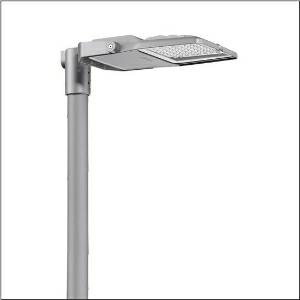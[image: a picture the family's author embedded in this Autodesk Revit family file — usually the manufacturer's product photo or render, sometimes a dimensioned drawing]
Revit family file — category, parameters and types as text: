
# Revit family: floodlight_fl_21_mini___pl33t_5xa7771d4f3a_f110
name_source: partatom
category: Lighting Fixtures
units: mm (PartAtom-declared; Revit-internal decimal feet)

## family parameters
Cut with Voids When Loaded = No
Host = Face
Light Source = No
Part Type = Normal
Room Calculation Point = No
Round Connector Dimension = Use Diameter
Shared = No

## types (1)
- --- (1 x LED, 18390 lm, 143 W, 4000K)
    Apparent Load = 143 VA
    CIE Flux Codes = 26 75 99 100 100
    Color Rendering = 70
    Color Temperature = 4000K
    Default Elevation = 1800 mm
    Description = Floodlight FL 21 mini, floodlight, primary light control with lens, of PMMA, primary optical cover: protective disc, of toughened safety glass, transparent, light distribution: PL33T, light emission: direct distribution, installation type: surface-mounted, LED, High Power LED, rated luminous flux: 18.390lm, luminous efficacy: 129lm/W, light colour: 740, colour temperature: 4000K, control gear: ECG iQ, control: Auto-Match, Temp-Guard, Lumen-Switch, Night-Set, Smart-Wire, Light-Fading, Desk-Remote (wireless, voltage-free reading and setting of iQ features in the workshop via application-optimized NFC function/RFID function), optimised constant luminous flux control (CLO 2.0), with terminal, 6-pole, mains connection: 220..240V, AC, 50/60Hz, start of lifetime: 143W, end of lifetime: 152W, reduction: 61W, luminaire housing, of diecast aluminium, powder-coated, Siteco® metallic grey (DB 702S), corrosivity category C5 according to DIN EN ISO 12944, mast bracket, of steel, galvanised, powder-coated, Siteco® metallic grey (DB 702S), protection rating (complete): IP66, insulation class (complete): insulation class II (safety insulation), certification: CE, ENEC, VDE, protection symbol: D, impact resistance: IK08, permissible operating ambient temperature: -40..+40°C, permissible operating ambient temperature for outdoor applications: -40..+50°C, standard: DIN EN 12944, packaging unit: 1 piece

Light Distribution: PL33T
    Height = 70 mm
    Lamp = 1 x LED
    Lamp Light Flux = 18390 lm
    Lamp Power = 143 W
    Lamp count = 1
    Length = 485 mm
    Luminous efficacy = 129 lm/W
    Manufacturer = Siteco
    ModVariant = No
    Model = 5XA7771D4F3A
    Number of Poles = 1
    OnlyDefault = Yes
    Power Factor = 1
    Product Name = Floodlight FL 21 mini | PL33T
    Product group = floodlight | pylon top
    ProductGroupID = 6101
    Protection Class = Protection class II
    Protection Degree = IP 66
    RLX_Detail_Level = 1
    RlxData = <blob elided: 101273 chars, md5=235de6cc>
    Socket = socket
    Standby Power = 0 W
    System Light Flux = 18390 lm
    System Power = 143 W
    Type Comments = factory setting: luminous flux: 100 % | dim-lin: 254 | 730 mA
    Type Image = l_1007125.jpg
    URL = http://relux.com
    VarID = @adj_059105
    Voltage = 0 V
    Weight = 0.00 kg
    Width = 337 mm

## geometry (parser evidence)
native form markers: Blend x4, Sweep x10
no freeform markers — native parametric forms only
